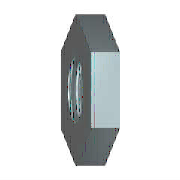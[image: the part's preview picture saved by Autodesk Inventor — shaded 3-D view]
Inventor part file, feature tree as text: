
AUTODESK INVENTOR PART (.ipt)
format: ipt  version: 2018 (Build 220112000, 112)  size: 134,144 bytes
history: native  units: mm (DEFAULTED — no unit token found)
features: other x4, sketch x2, extrude x1, chamfer x1
ambient origin geometry x8: Origin, YZ Plane, XZ Plane, XY Plane, X Axis, Y Axis, Z Axis, Center Point
bodies: Solid1 (feature_tree)
feature tree (8):
  extrude  "Extrusion1"  TaperAngle=0.0deg  [1 undecoded]
  other  "MSC_A1"
  other  "MSC_PT1"
  other  "MSC_PT2"
  other  "MSC_PF1"
  chamfer  "Chamfer1"  [1 undecoded]
  sketch  "Sketch1"  dims[d2=0.0mm]
  sketch  "Sketch2"  dims[d3=4.134mm d4=2.7mm d5=4.0mm d6=2.0mm d7=60.0deg d8=8.0mm d9=20.594885mm d14=0.0mm d15=0.0mm d16=0.0mm d17=0.48mm d18=0.48mm d20=45.0deg d21=0.0mm d23=0.0mm d24=0.0mm d25=0.0mm]
note: 2 required parameter values undecoded (feature->parameter linkage not recoverable at this tier; creation-order binding heuristic only, values carry confidence <= 0.55)
